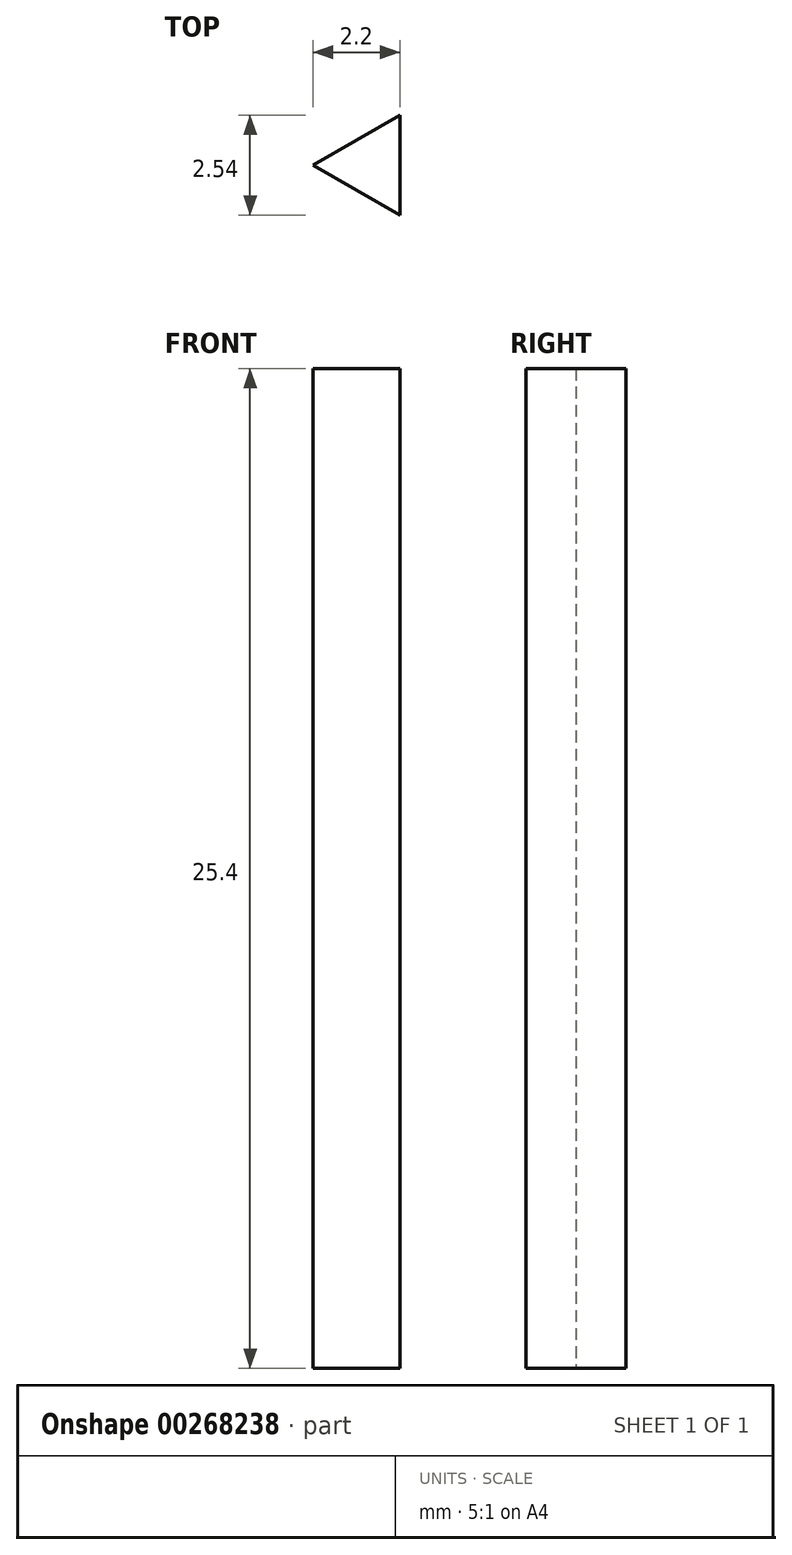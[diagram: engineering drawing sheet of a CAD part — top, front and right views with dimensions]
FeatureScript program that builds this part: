
annotation { "Feature Type Name" : "Feature", "Feature Type Description" : "" }
export const myFeature = defineFeature(function(context is Context, id is Id, definition is map)
    precondition{}
    {
        {
            var Q0;
            Q0=qCreatedBy(makeId("Top.planeOp"),FACE);
            var sketch = newSketch(context, id + "F0", { "sketchPlane" : qUnion([Q0])});
            skLineSegment(sketch, "E0", {"start": v(-38.55, -37.09) * mm, "end": v(-36.35, -38.36) * mm});
            skLineSegment(sketch, "E1", {"start": v(-36.35, -38.36) * mm, "end": v(-36.35, -35.82) * mm});
            skLineSegment(sketch, "E2", {"start": v(-36.35, -35.82) * mm, "end": v(-38.55, -37.09) * mm});
            skSolve(sketch);
        }
        {
            var Q0;
            Q0 = qSketchRegion(id + "F0", true);
            extrude(context, id + "F1", {"entities" : qUnion([Q0]), "depth" : 25.4 * mm});
        }
        {
            var Q0;
            Q0=qCreatedBy(makeId("Front.planeOp"),FACE);
            var sketch = newSketch(context, id + "F2", { "sketchPlane" : qUnion([Q0])});
            skLineSegment(sketch, "E3", {"start": v(-54.49, -36.24) * mm, "end": v(-13.61, -59.83) * mm});
            skLineSegment(sketch, "E4", {"start": v(-13.61, -59.83) * mm, "end": v(-13.61, -12.64) * mm});
            skLineSegment(sketch, "E5", {"start": v(-13.61, -12.64) * mm, "end": v(-54.49, -36.24) * mm});
            skLineSegment(sketch, "E6", {"start": v(-49.4, -36.24) * mm, "end": v(-16.15, -17.04) * mm});
            skLineSegment(sketch, "E7", {"start": v(-16.15, -17.04) * mm, "end": v(-16.15, -55.43) * mm});
            skLineSegment(sketch, "E8", {"start": v(-16.15, -55.43) * mm, "end": v(-49.4, -36.24) * mm});
            skLineSegment(sketch, "E9", {"start": v(-54.49, -36.24) * mm, "end": v(-49.4, -36.24) * mm});
            skLineSegment(sketch, "E10", {"start": v(-16.15, -17.04) * mm, "end": v(-13.61, -12.64) * mm});
            skLineSegment(sketch, "E11", {"start": v(-16.15, -55.43) * mm, "end": v(-13.61, -59.83) * mm});
            skSolve(sketch);
        }
        {
            var Q0;
            Q0=sQuery(id+"F2.wireOp",EDGE,"E4");
            var Q1;
            Q1=sQuery(id+"F2.wireOp",EDGE,"E3");
            var Q2;
            Q2=sQuery(id+"F2.wireOp",EDGE,"E5");
            extrude(context, id + "F3", {"bodyType" : ToolBodyType.SURFACE, "surfaceEntities" : qUnion([Q0, Q1, Q2]), "endBound" : BoundingType.SYMMETRIC, "depth" : 5.08 * mm});
        }
    });
